# Revit family: Gira_029527
name_source: partatom
category: Elektroinstallationen
revit_build: Autodesk Revit 2017 (Build: 20160225_1515(x64)
units: mm (PartAtom-declared; Revit-internal decimal feet)

## family parameters
Basisbauteil = Fläche
Beim Laden mit Abzugskörper schneiden = Nein
Bemaßung runder Anschluss = Durchmesser verwenden
Beschriftungsausrichtung beibehalten = Nein
Gemeinsam genutzt = Nein
Raumberechnungspunkt = Nein
Teiletyp = Normal

## types (1)
- Gira_029527
    BIM = https://media.stage.bim.site und Tasten.rfa
    Beschreibung = Rock.2g Sys55 PWm,Rocker, 2-gang,,pure white matt,
    Colour = White
    Data sheet = https://katalog.gira.de
    GTIN = 4010337295273
    HAN = 029527
    Halogen free = Ja
    Hersteller = Gira
    Imprint/indication = Without imprint
    Material = Plastic
    Material quality = Thermoplastic
    Model = Two-part rocker
    Monitoring window/light outlet = Nein
    Productwebsite = http://katalog.gira.de
    RAL-number (akin) = 9010
    Scannable symbol / barrier free = Nein
    Suitable for degree of protection (IP) = IP20
    Suitable for touch sensor connector for bus system = Ja
    Surface finishing = Matt
    Surface protection = Other
    Type of fastening = Clamp mounting
    Typname = Rocker 2-g System 55 p.white m
    URL = https://www.gira.de
    Utilization = Switch/push button
    Vorgabe-Ansicht = 1219 mm
    With exchangeable lens/symbol = Nein
    With label area = Nein

## geometry (parser evidence)
native form markers: Sweep x4
no freeform markers — native parametric forms only
